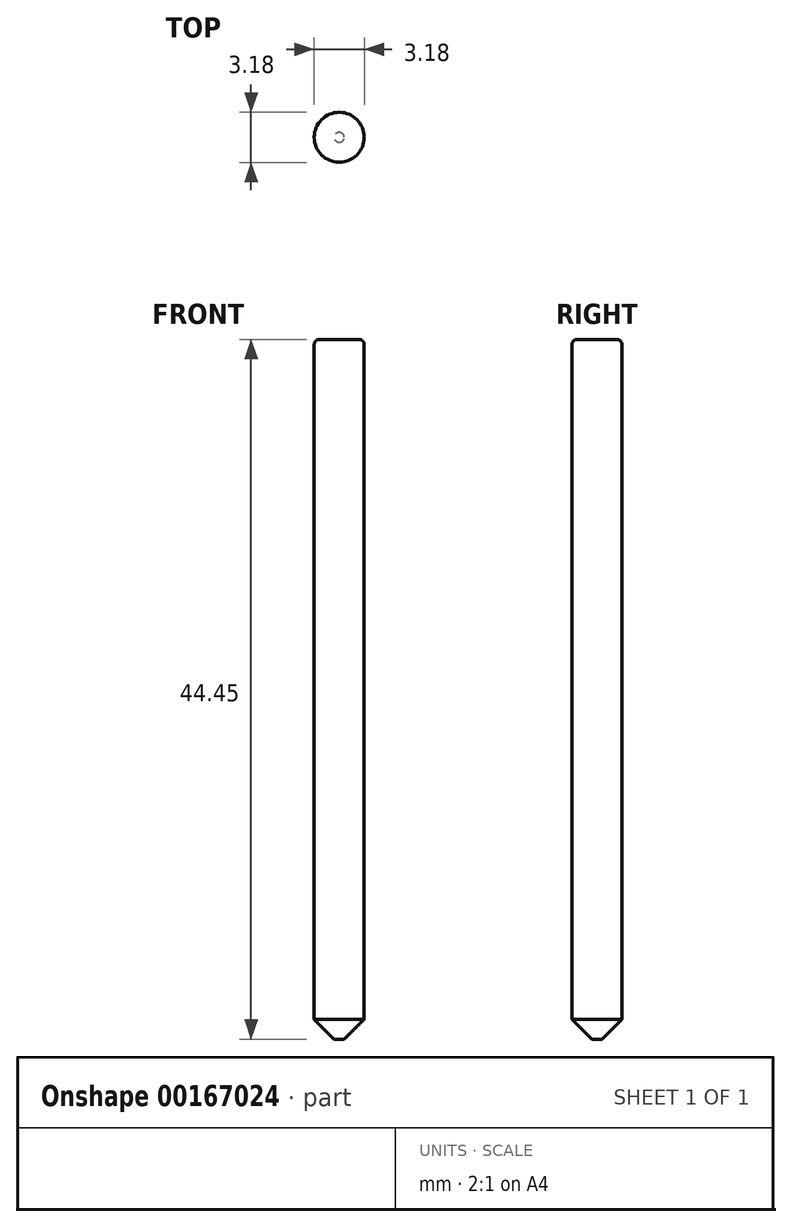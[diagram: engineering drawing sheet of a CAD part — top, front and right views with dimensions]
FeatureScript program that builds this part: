
annotation { "Feature Type Name" : "Feature", "Feature Type Description" : "" }
export const myFeature = defineFeature(function(context is Context, id is Id, definition is map)
    precondition{}
    {
        {
            var Q0;
            Q0=qCreatedBy(makeId("Top.planeOp"),FACE);
            var sketch = newSketch(context, id + "F0", { "sketchPlane" : qUnion([Q0])});
            skCircle(sketch, "E0", {"center": v(0, 0) * mm, "radius": 1.59 * mm});
            skSolve(sketch);
        }
        {
            var Q0;
            Q0=makeQuery(id+"F0.imprint","IMPRINT",FACE,{"disambiguationData":[TD([[makeQuery(id+"F0.imprint","IMPRINT",EDGE,{"derivedFrom":sQuery(id+"F0.wireOp",EDGE,"E0")}),1.0]])]});
            extrude(context, id + "F1", {"entities" : qUnion([Q0]), "depth" : 44.45 * mm});
        }
        {
            var Q0;
            Q0=makeQuery(id+"F1.opExtrude","CAP_FACE",FACE,{"disambiguationData":[OSD([sQuery(id+"F0.wireOp",EDGE,"E0")])],"isStart":false});
            var sketch = newSketch(context, id + "F2", { "sketchPlane" : qUnion([Q0])});
            skSolve(sketch);
        }
        {
            var Q0;
            Q0=makeQuery(id+"F1.opExtrude","CAP_EDGE",EDGE,{"disambiguationData":[OSD([sQuery(id+"F0.wireOp",EDGE,"E0")])],"isStart":true});
            chamfer(context, id + "F3", {"entities" : qUnion([Q0]), "width" : 1.27 * mm, "tangentPropagation" : true});
        }
        {
            var Q0;
            Q0=makeQuery(id+"F1.opExtrude","CAP_EDGE",EDGE,{"disambiguationData":[OSD([sQuery(id+"F0.wireOp",EDGE,"E0")])],"isStart":false});
            fillet(context, id + "F4", {"entities" : qUnion([Q0]), "radius" : 0.32 * mm, "tangentPropagation" : true, "allowEdgeOverflow" : false});
        }
    });
